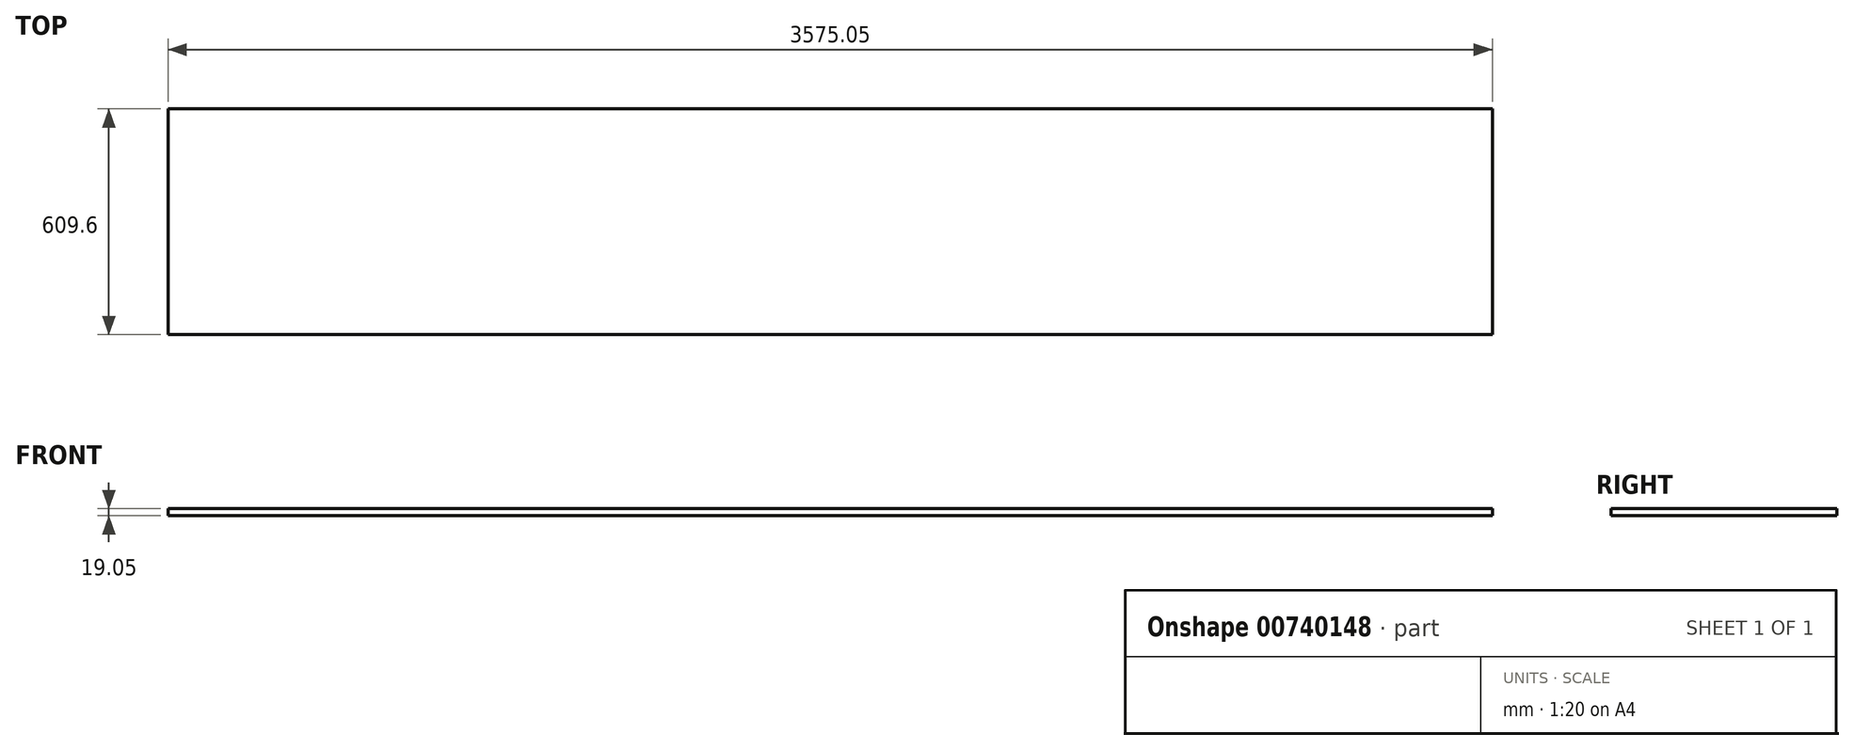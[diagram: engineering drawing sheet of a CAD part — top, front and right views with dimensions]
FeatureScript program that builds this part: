
annotation { "Feature Type Name" : "Feature", "Feature Type Description" : "" }
export const myFeature = defineFeature(function(context is Context, id is Id, definition is map)
    precondition{}
    {
        {
            var Q0;
            Q0=qCreatedBy(makeId("Top.planeOp"),FACE);
            var sketch = newSketch(context, id + "F0", { "sketchPlane" : qUnion([Q0])});
            skLineSegment(sketch, "E0.bottom", {"start": v(-897.52, 160.32) * mm, "end": v(2677.53, 160.32) * mm});
            skLineSegment(sketch, "E0.top", {"start": v(-897.52, -449.28) * mm, "end": v(2677.53, -449.28) * mm});
            skLineSegment(sketch, "E0.left", {"start": v(-897.52, 160.32) * mm, "end": v(-897.52, -449.28) * mm});
            skLineSegment(sketch, "E0.right", {"start": v(2677.53, 160.32) * mm, "end": v(2677.53, -449.28) * mm});
            skSolve(sketch);
        }
        {
            var Q0;
            Q0=makeQuery(id+"F0.imprint","IMPRINT",FACE,{"disambiguationData":[TD([[makeQuery(id+"F0.imprint","IMPRINT",EDGE,{"derivedFrom":sQuery(id+"F0.wireOp",EDGE,"E0.bottom")}),-1.0]])]});
            extrude(context, id + "F1", {"entities" : qUnion([Q0]), "depth" : 19.05 * mm, "offsetDistance" : 25.4 * mm});
        }
    });
